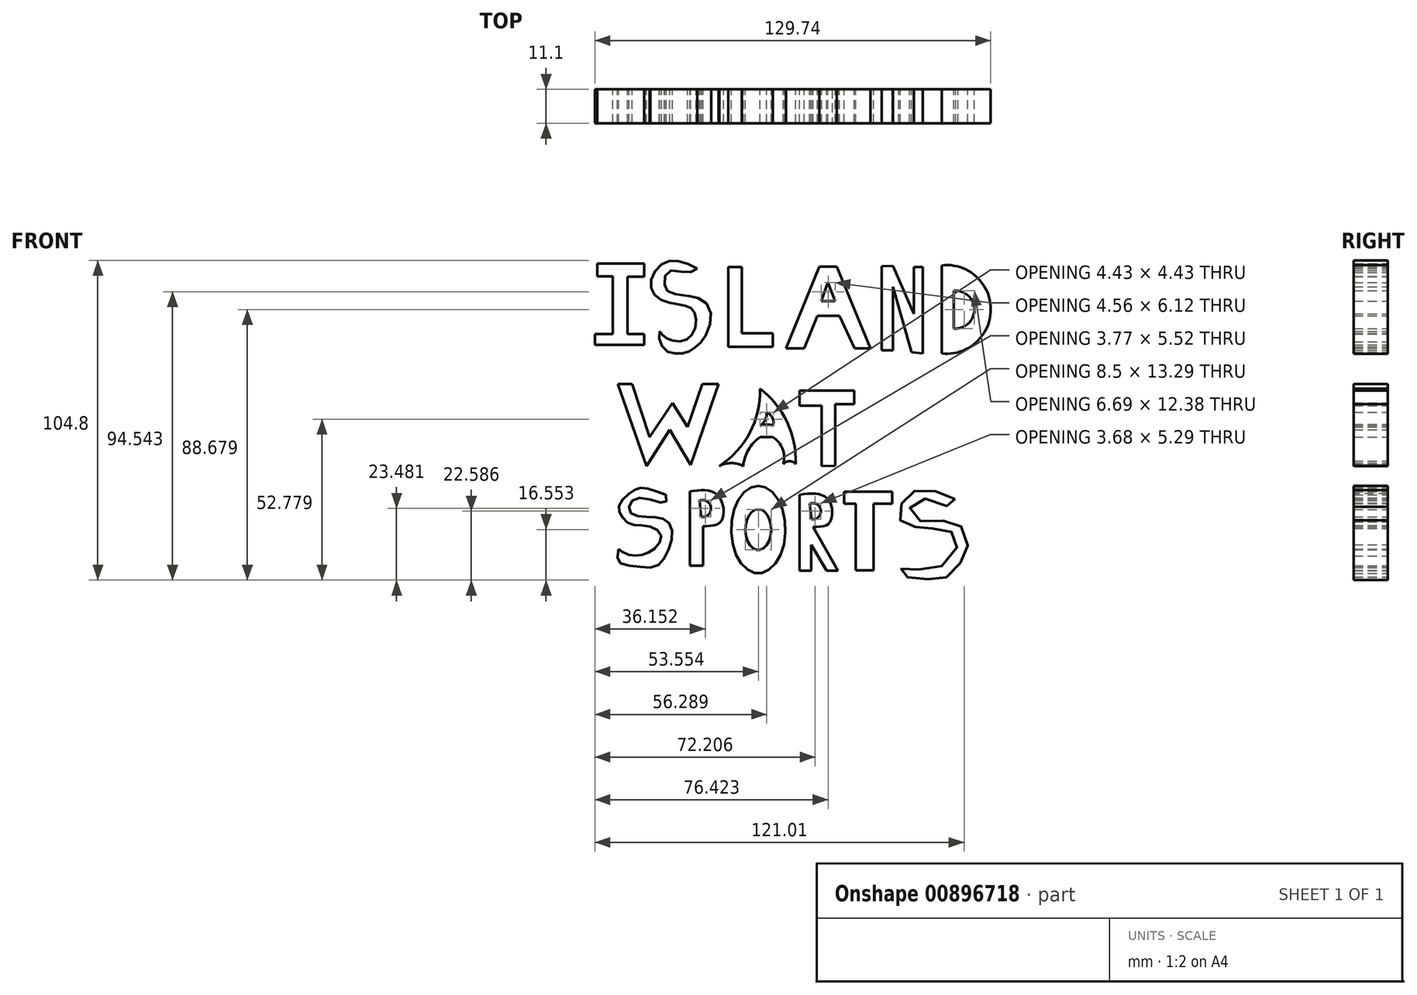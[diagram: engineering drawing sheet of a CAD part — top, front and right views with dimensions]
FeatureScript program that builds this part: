
annotation { "Feature Type Name" : "Feature", "Feature Type Description" : "" }
export const myFeature = defineFeature(function(context is Context, id is Id, definition is map)
    precondition{}
    {
        {
            var Q0;
            Q0=qCreatedBy(makeId("Front.planeOp"),FACE);
            var sketch = newSketch(context, id + "F0", { "sketchPlane" : qUnion([Q0])});
            skLineSegment(sketch, "E0", {"start": v(-52.45, 52.71) * mm, "end": v(-52.45, 33.82) * mm});
            skLineSegment(sketch, "E1", {"start": v(-52.45, 33.82) * mm, "end": v(-58.31, 33.82) * mm});
            skLineSegment(sketch, "E2", {"start": v(-58.31, 33.82) * mm, "end": v(-58.31, 30.3) * mm});
            skLineSegment(sketch, "E3", {"start": v(-58.31, 30.3) * mm, "end": v(-42.16, 30.3) * mm});
            skLineSegment(sketch, "E4", {"start": v(-42.16, 30.3) * mm, "end": v(-42.16, 33.82) * mm});
            skLineSegment(sketch, "E5", {"start": v(-42.16, 33.82) * mm, "end": v(-47.63, 33.82) * mm});
            skLineSegment(sketch, "E6", {"start": v(-47.63, 33.82) * mm, "end": v(-47.63, 52.58) * mm});
            skLineSegment(sketch, "E7", {"start": v(-47.63, 52.58) * mm, "end": v(-42.16, 52.58) * mm});
            skLineSegment(sketch, "E8", {"start": v(-52.45, 52.71) * mm, "end": v(-57.53, 52.71) * mm});
            skLineSegment(sketch, "E9", {"start": v(-57.53, 52.71) * mm, "end": v(-57.53, 56.88) * mm});
            skLineSegment(sketch, "E10", {"start": v(-57.53, 56.88) * mm, "end": v(-42.16, 56.88) * mm});
            skLineSegment(sketch, "E11", {"start": v(-42.16, 56.88) * mm, "end": v(-42.16, 52.58) * mm});
            skFitSpline(sketch, "E12", {"points": [v(-24.82, 55.32) * mm, v(-34.47, 57.66) * mm, v(-40.07, 50.63) * mm, v(-36.55, 45.02) * mm, v(-29, 43.2) * mm, v(-25.6, 40.85) * mm, v(-26, 34.34) * mm, v(-30.56, 31.34) * mm, v(-35.5, 32.9) * mm, v(-37.07, 34.73) * mm], "startDerivative": vector(-70.48, 35.1) * mm, "endDerivative": vector(-16.93, 26.6) * mm});
            skFitSpline(sketch, "E13", {"points": [v(-37.07, 34.73) * mm, v(-37.07, 31.34) * mm, v(-34.6, 28.08) * mm, v(-31.34, 27.43) * mm, v(-28.34, 27.7) * mm, v(-25.21, 29.65) * mm, v(-23, 31.73) * mm, v(-20.26, 38.77) * mm, v(-22.6, 44.63) * mm, v(-27.7, 46.33) * mm, v(-29.78, 46.59) * mm, v(-34.2, 47.63) * mm, v(-35.5, 50.36) * mm, v(-34.2, 54.4) * mm, v(-27.95, 54.01) * mm, v(-24.82, 55.32) * mm], "startDerivative": vector(-8.29, -55.15) * mm, "endDerivative": vector(42.75, 32.05) * mm});
            skLineSegment(sketch, "E14", {"start": v(-14.66, 55.84) * mm, "end": v(-14.66, 29.65) * mm});
            skLineSegment(sketch, "E15", {"start": v(-14.66, 29.65) * mm, "end": v(0, 29.65) * mm});
            skLineSegment(sketch, "E16", {"start": v(0, 29.65) * mm, "end": v(0, 34.08) * mm});
            skLineSegment(sketch, "E17", {"start": v(0, 34.08) * mm, "end": v(-10.23, 34.08) * mm});
            skLineSegment(sketch, "E18", {"start": v(-10.23, 34.08) * mm, "end": v(-10.23, 55.84) * mm});
            skLineSegment(sketch, "E19", {"start": v(-10.23, 55.84) * mm, "end": v(-14.66, 55.84) * mm});
            skLineSegment(sketch, "E20", {"start": v(15.18, 55.97) * mm, "end": v(4.37, 29.12) * mm});
            skLineSegment(sketch, "E21", {"start": v(4.37, 29.12) * mm, "end": v(10.23, 29.12) * mm});
            skLineSegment(sketch, "E22", {"start": v(10.23, 29.12) * mm, "end": v(14.66, 39.8) * mm});
            skLineSegment(sketch, "E23", {"start": v(14.66, 39.8) * mm, "end": v(21.83, 39.8) * mm});
            skLineSegment(sketch, "E24", {"start": v(21.83, 39.8) * mm, "end": v(26.78, 29.12) * mm});
            skLineSegment(sketch, "E25", {"start": v(26.78, 29.12) * mm, "end": v(32, 29.12) * mm});
            skLineSegment(sketch, "E26", {"start": v(32, 29.12) * mm, "end": v(20.91, 55.97) * mm});
            skLineSegment(sketch, "E27", {"start": v(20.91, 55.97) * mm, "end": v(15.18, 55.97) * mm});
            skLineSegment(sketch, "E28", {"start": v(15.83, 44.63) * mm, "end": v(20.4, 44.63) * mm});
            skLineSegment(sketch, "E29", {"start": v(20.4, 44.63) * mm, "end": v(18.05, 50.76) * mm});
            skLineSegment(sketch, "E30", {"start": v(18.05, 50.76) * mm, "end": v(15.83, 44.63) * mm});
            skLineSegment(sketch, "E31", {"start": v(35.64, 56.1) * mm, "end": v(35.64, 28.47) * mm});
            skLineSegment(sketch, "E32", {"start": v(35.64, 28.47) * mm, "end": v(39.42, 28.47) * mm});
            skLineSegment(sketch, "E33", {"start": v(39.42, 28.47) * mm, "end": v(39.42, 49.32) * mm});
            skLineSegment(sketch, "E34", {"start": v(49.2, 27.43) * mm, "end": v(49.2, 55.84) * mm});
            skLineSegment(sketch, "E35", {"start": v(49.2, 55.84) * mm, "end": v(46.2, 55.84) * mm});
            skLineSegment(sketch, "E36", {"start": v(46.2, 55.84) * mm, "end": v(46.2, 40.46) * mm});
            skLineSegment(sketch, "E37", {"start": v(46.2, 40.46) * mm, "end": v(39.42, 56.23) * mm});
            skLineSegment(sketch, "E38", {"start": v(39.42, 56.23) * mm, "end": v(35.64, 56.1) * mm});
            skLineSegment(sketch, "E39", {"start": v(39.42, 49.32) * mm, "end": v(45.41, 27.82) * mm});
            skLineSegment(sketch, "E40", {"start": v(45.41, 27.82) * mm, "end": v(49.2, 27.43) * mm});
            skLineSegment(sketch, "E41", {"start": v(55.32, 56.36) * mm, "end": v(55.32, 27.43) * mm});
            skArc(sketch, "E42", {"start": v(55.32, 27.43) * mm, "mid": v(71.43, 41.9) * mm, "end": v(55.32, 56.36) * mm});
            skLineSegment(sketch, "E43", {"start": v(59.36, 48.02) * mm, "end": v(59.36, 35.64) * mm});
            skArc(sketch, "E44", {"start": v(59.36, 35.64) * mm, "mid": v(66.04, 41.83) * mm, "end": v(59.36, 48.02) * mm});
            skLineSegment(sketch, "E45", {"start": v(-41.37, -9.45) * mm, "end": v(-33.82, 2.41) * mm});
            skLineSegment(sketch, "E46", {"start": v(-33.82, 2.41) * mm, "end": v(-26.9, -9.06) * mm});
            skLineSegment(sketch, "E47", {"start": v(-26.9, -9.06) * mm, "end": v(-17.79, 17.4) * mm});
            skLineSegment(sketch, "E48", {"start": v(-17.79, 17.4) * mm, "end": v(-23.13, 17.4) * mm});
            skLineSegment(sketch, "E49", {"start": v(-23.13, 17.4) * mm, "end": v(-27.98, 3.34) * mm});
            skLineSegment(sketch, "E50", {"start": v(-27.98, 3.34) * mm, "end": v(-32.9, 11.27) * mm});
            skLineSegment(sketch, "E51", {"start": v(-32.9, 11.27) * mm, "end": v(-40.33, 0) * mm});
            skLineSegment(sketch, "E52", {"start": v(-40.33, 0) * mm, "end": v(-46.06, 17.4) * mm});
            skLineSegment(sketch, "E53", {"start": v(-41.37, -9.45) * mm, "end": v(-50.76, 17.4) * mm});
            skLineSegment(sketch, "E54", {"start": v(-50.76, 17.4) * mm, "end": v(-46.06, 17.4) * mm});
            skArc(sketch, "E55", {"start": v(-17.53, -9.45) * mm, "mid": v(-7.52, 1.5) * mm, "end": v(-4.24, 15.96) * mm});
            skArc(sketch, "E56", {"start": v(7.5, -8.8) * mm, "mid": v(4.64, 5.01) * mm, "end": v(-4.24, 15.96) * mm});
            skArc(sketch, "E57", {"start": v(-9.7, -9.45) * mm, "mid": v(-13.62, -8.5) * mm, "end": v(-17.53, -9.45) * mm});
            skArc(sketch, "E58", {"start": v(-4.24, 0) * mm, "mid": v(-8, -4.13) * mm, "end": v(-9.7, -9.45) * mm});
            skLineSegment(sketch, "E59", {"start": v(-4.24, 0) * mm, "end": v(0, 0) * mm});
            skArc(sketch, "E60", {"start": v(3.45, -8.8) * mm, "mid": v(3.2, -3.82) * mm, "end": v(0, 0) * mm});
            skArc(sketch, "E61", {"start": v(7.5, -8.8) * mm, "mid": v(5.47, -7.88) * mm, "end": v(3.45, -8.8) * mm});
            skArc(sketch, "E62", {"start": v(-4.24, 3.71) * mm, "mid": v(-2.5, 5.62) * mm, "end": v(-2.02, 8.14) * mm});
            skArc(sketch, "E63", {"start": v(0, 3.71) * mm, "mid": v(-2.12, 4.17) * mm, "end": v(-4.24, 3.71) * mm});
            skArc(sketch, "E64", {"start": v(0, 3.71) * mm, "mid": v(-0.12, 6.34) * mm, "end": v(-2.02, 8.14) * mm});
            skLineSegment(sketch, "E65", {"start": v(15.96, -9.45) * mm, "end": v(15.96, 10.36) * mm});
            skLineSegment(sketch, "E66", {"start": v(15.96, 10.36) * mm, "end": v(8.8, 10.36) * mm});
            skLineSegment(sketch, "E67", {"start": v(8.8, 10.36) * mm, "end": v(8.8, 15.31) * mm});
            skLineSegment(sketch, "E68", {"start": v(8.8, 15.31) * mm, "end": v(26.65, 15.31) * mm});
            skLineSegment(sketch, "E69", {"start": v(26.65, 15.31) * mm, "end": v(26.65, 10.88) * mm});
            skLineSegment(sketch, "E70", {"start": v(26.65, 10.88) * mm, "end": v(20.4, 10.88) * mm});
            skLineSegment(sketch, "E71", {"start": v(20.4, 10.88) * mm, "end": v(20.4, -9.32) * mm});
            skLineSegment(sketch, "E72", {"start": v(20.4, -9.32) * mm, "end": v(15.96, -9.45) * mm});
            skLineSegment(sketch, "E73", {"start": v(30.56, 15.57) * mm, "end": v(30.56, -8.93) * mm});
            skLineSegment(sketch, "E74", {"start": v(30.56, -8.93) * mm, "end": v(40.6, -8.93) * mm});
            skLineSegment(sketch, "E75", {"start": v(40.6, -8.93) * mm, "end": v(40.6, -3.45) * mm});
            skLineSegment(sketch, "E76", {"start": v(40.6, -3.45) * mm, "end": v(34.2, -3.45) * mm});
            skLineSegment(sketch, "E77", {"start": v(34.2, -3.45) * mm, "end": v(34.2, 2.54) * mm});
            skLineSegment(sketch, "E78", {"start": v(34.2, 2.54) * mm, "end": v(39.03, 2.54) * mm});
            skLineSegment(sketch, "E79", {"start": v(39.03, 2.54) * mm, "end": v(39.03, 7.36) * mm});
            skLineSegment(sketch, "E80", {"start": v(39.03, 7.36) * mm, "end": v(34.08, 7.36) * mm});
            skLineSegment(sketch, "E81", {"start": v(34.08, 7.36) * mm, "end": v(34.08, 11.27) * mm});
            skLineSegment(sketch, "E82", {"start": v(34.08, 11.27) * mm, "end": v(40.6, 11.27) * mm});
            skLineSegment(sketch, "E83", {"start": v(40.6, 11.27) * mm, "end": v(40.6, 15.57) * mm});
            skLineSegment(sketch, "E84", {"start": v(40.6, 15.57) * mm, "end": v(30.56, 15.57) * mm});
            skLineSegment(sketch, "E85", {"start": v(44.9, 15.57) * mm, "end": v(44.9, -9.45) * mm});
            skLineSegment(sketch, "E86", {"start": v(44.9, -9.45) * mm, "end": v(44.9, 15.57) * mm});
            skFitSpline(sketch, "E87", {"points": [v(44.9, 15.57) * mm, v(50.5, 15.57) * mm, v(55.84, 12.05) * mm, v(58.57, 7.1) * mm, v(58.57, 2.8) * mm, v(53.75, 0) * mm, v(49.2, 0) * mm, v(49.45, 0) * mm], "startDerivative": vector(34.15, 4.52) * mm, "endDerivative": vector(11.25, -0.37) * mm});
            skLineSegment(sketch, "E88", {"start": v(49.45, 0) * mm, "end": v(57.14, -9.7) * mm});
            skLineSegment(sketch, "E89", {"start": v(57.14, -9.7) * mm, "end": v(51.54, -9.7) * mm});
            skLineSegment(sketch, "E90", {"start": v(51.54, -9.7) * mm, "end": v(48.02, -3.58) * mm});
            skLineSegment(sketch, "E91", {"start": v(48.02, -3.58) * mm, "end": v(48.02, -9.45) * mm});
            skLineSegment(sketch, "E92", {"start": v(48.02, -9.45) * mm, "end": v(44.9, -9.45) * mm});
            skArc(sketch, "E93", {"start": v(49.45, 4.1) * mm, "mid": v(53.9, 8) * mm, "end": v(49.58, 12.05) * mm});
            skLineSegment(sketch, "E94", {"start": v(49.58, 12.05) * mm, "end": v(49.45, 4.1) * mm});
            skFitSpline(sketch, "E95", {"points": [v(-35.12, -18.83) * mm, v(-42.55, -16.61) * mm, v(-46.2, -17.79) * mm, v(-50.36, -22.22) * mm, v(-49.84, -25.35) * mm, v(-46.59, -28.6) * mm, v(-40.72, -29.12) * mm, v(-36.55, -32.38) * mm, v(-38.9, -36.68) * mm, v(-43.2, -38.64) * mm, v(-47.5, -38.5) * mm, v(-50.5, -36.68) * mm, v(-50.5, -36.55) * mm], "startDerivative": vector(-72.28, 27.88) * mm, "endDerivative": vector(3.28, 7.09) * mm});
            skFitSpline(sketch, "E96", {"points": [v(-50.5, -36.55) * mm, v(-50.5, -40.85) * mm, v(-44.76, -42.42) * mm, v(-38.25, -42.29) * mm, v(-34.86, -38.25) * mm, v(-32.9, -31.34) * mm, v(-34.6, -27.56) * mm, v(-38.64, -26.26) * mm, v(-43.98, -25.87) * mm, v(-46.98, -24.3) * mm, v(-46.33, -21.04) * mm, v(-41.63, -20.13) * mm, v(-35.25, -21.44) * mm, v(-35.12, -18.83) * mm], "startDerivative": vector(-15.68, -68.6) * mm, "endDerivative": vector(-12.3, 59.6) * mm});
            skLineSegment(sketch, "E97", {"start": v(-27.17, -17.79) * mm, "end": v(-27.17, -42.16) * mm});
            skLineSegment(sketch, "E98", {"start": v(-27.17, -42.16) * mm, "end": v(-22.87, -42.16) * mm});
            skLineSegment(sketch, "E99", {"start": v(-22.87, -42.16) * mm, "end": v(-22.87, -29.12) * mm});
            skFitSpline(sketch, "E100", {"points": [v(-22.87, -29.12) * mm, v(-17.14, -27.82) * mm, v(-16.48, -21.96) * mm, v(-20, -17.79) * mm, v(-27.17, -17.79) * mm], "startDerivative": vector(27.8, 0.19) * mm, "endDerivative": vector(-28.78, -4.2) * mm});
            skArc(sketch, "E101", {"start": v(-23.52, -26.13) * mm, "mid": v(-20.27, -23.11) * mm, "end": v(-24.04, -20.78) * mm});
            skLineSegment(sketch, "E102", {"start": v(-24.04, -20.78) * mm, "end": v(-23.52, -26.13) * mm});
            skEllipse(sketch, "E103", {"center": v(-4.76, -30.3) * mm, "majorRadius": 14.33 * mm, "minorRadius": 8.9 * mm, "majorAxis": v(0, 1)});
            skEllipse(sketch, "E104", {"center": v(-4.76, -30.3) * mm, "majorRadius": 6.65 * mm, "minorRadius": 4.25 * mm, "majorAxis": v(0, 1)});
            skLineSegment(sketch, "E105", {"start": v(8.8, -18.83) * mm, "end": v(8.8, -43.72) * mm});
            skLineSegment(sketch, "E106", {"start": v(8.8, -43.72) * mm, "end": v(12.57, -43.72) * mm});
            skLineSegment(sketch, "E107", {"start": v(12.57, -43.72) * mm, "end": v(12.57, -35.25) * mm});
            skLineSegment(sketch, "E108", {"start": v(12.57, -35.25) * mm, "end": v(17.66, -43.72) * mm});
            skLineSegment(sketch, "E109", {"start": v(17.66, -43.72) * mm, "end": v(21.3, -43.72) * mm});
            skLineSegment(sketch, "E110", {"start": v(21.3, -43.72) * mm, "end": v(13.23, -29.38) * mm});
            skFitSpline(sketch, "E111", {"points": [v(8.8, -18.83) * mm, v(15.7, -18.83) * mm, v(18.96, -21.83) * mm, v(19.35, -25.87) * mm, v(18.05, -28.6) * mm, v(13.23, -29.38) * mm], "startDerivative": vector(30.5, 3.96) * mm, "endDerivative": vector(-27.36, -0.32) * mm});
            skArc(sketch, "E112", {"start": v(12.7, -26.9) * mm, "mid": v(15.74, -23.94) * mm, "end": v(12.05, -21.83) * mm});
            skLineSegment(sketch, "E113", {"start": v(12.05, -21.83) * mm, "end": v(12.7, -26.9) * mm});
            skLineSegment(sketch, "E114", {"start": v(27.17, -21.83) * mm, "end": v(27.17, -43.59) * mm});
            skLineSegment(sketch, "E115", {"start": v(27.17, -43.59) * mm, "end": v(33.03, -43.59) * mm});
            skLineSegment(sketch, "E116", {"start": v(33.03, -43.59) * mm, "end": v(33.03, -21.83) * mm});
            skLineSegment(sketch, "E117", {"start": v(33.03, -21.83) * mm, "end": v(39.16, -21.83) * mm});
            skLineSegment(sketch, "E118", {"start": v(39.16, -21.83) * mm, "end": v(39.16, -17.92) * mm});
            skLineSegment(sketch, "E119", {"start": v(39.16, -17.92) * mm, "end": v(23.4, -17.92) * mm});
            skLineSegment(sketch, "E120", {"start": v(23.4, -17.92) * mm, "end": v(23.4, -21.83) * mm});
            skLineSegment(sketch, "E121", {"start": v(23.4, -21.83) * mm, "end": v(27.17, -21.83) * mm});
            skFitSpline(sketch, "E122", {"points": [v(59.75, -20.26) * mm, v(52.58, -17.66) * mm, v(45.8, -17.92) * mm, v(42.02, -22.22) * mm, v(41.63, -27.04) * mm, v(45.41, -29.12) * mm, v(50.1, -29.9) * mm, v(55.97, -30.17) * mm, v(60.53, -33.03) * mm, v(57.92, -40.07) * mm, v(49.58, -43.72) * mm, v(42.68, -42.55) * mm, v(42.02, -45.54) * mm, v(46.46, -45.8) * mm, v(53.36, -46.85) * mm, v(58.44, -44.76) * mm, v(62.74, -39.16) * mm, v(63.79, -33.68) * mm, v(60, -27.82) * mm, v(52.97, -27.7) * mm, v(45.8, -26.13) * mm, v(45.54, -21.7) * mm, v(52.71, -20.65) * mm, v(58.7, -22.74) * mm, v(59.75, -20.26) * mm]});
            skLineSegment(sketch, "E123", {"start": v(-63.79, 62.74) * mm, "end": v(-62.48, -51.54) * mm});
            skLineSegment(sketch, "E124", {"start": v(-62.48, -51.54) * mm, "end": v(74.47, -52.71) * mm});
            skLineSegment(sketch, "E125", {"start": v(74.47, -52.71) * mm, "end": v(74.47, 61.44) * mm});
            skLineSegment(sketch, "E126", {"start": v(74.47, 61.44) * mm, "end": v(-63.79, 62.74) * mm});
            skArc(sketch, "E127", {"start": v(-63.79, 62.74) * mm, "mid": v(-55.89, 69.4) * mm, "end": v(-50.52, 78.22) * mm});
            skArc(sketch, "E128", {"start": v(-52.25, 62.64) * mm, "mid": v(-48.35, 70.1) * mm, "end": v(-50.52, 78.22) * mm});
            skArc(sketch, "E129", {"start": v(-52.25, 62.64) * mm, "mid": v(-41.84, 67.83) * mm, "end": v(-36.25, 78.03) * mm});
            skArc(sketch, "E130", {"start": v(-36.25, 62.64) * mm, "mid": v(-33.31, 70.33) * mm, "end": v(-36.25, 78.03) * mm});
            skArc(sketch, "E131", {"start": v(-36.25, 62.64) * mm, "mid": v(-24.78, 67.64) * mm, "end": v(-17.81, 78.03) * mm});
            skArc(sketch, "E132", {"start": v(-20.02, 62.33) * mm, "mid": v(-16.4, 69.83) * mm, "end": v(-17.81, 78.03) * mm});
            skArc(sketch, "E133", {"start": v(-20.02, 62.33) * mm, "mid": v(-8.26, 66.4) * mm, "end": v(-3.83, 78.03) * mm});
            skArc(sketch, "E134", {"start": v(0, 62.33) * mm, "mid": v(0.66, 70.81) * mm, "end": v(-3.83, 78.03) * mm});
            skArc(sketch, "E135", {"start": v(0, 62.33) * mm, "mid": v(8.7, 68.15) * mm, "end": v(12.16, 78.03) * mm});
            skArc(sketch, "E136", {"start": v(16, 62) * mm, "mid": v(16.7, 70.64) * mm, "end": v(12.16, 78.03) * mm});
            skArc(sketch, "E137", {"start": v(16, 62) * mm, "mid": v(24.7, 67.87) * mm, "end": v(29.48, 77.22) * mm});
            skArc(sketch, "E138", {"start": v(31.14, 61.85) * mm, "mid": v(33.3, 69.85) * mm, "end": v(29.48, 77.22) * mm});
            skArc(sketch, "E139", {"start": v(31.14, 61.85) * mm, "mid": v(38.47, 67.25) * mm, "end": v(41.67, 75.78) * mm});
            skArc(sketch, "E140", {"start": v(45.15, 61.72) * mm, "mid": v(45, 69.14) * mm, "end": v(41.67, 75.78) * mm});
            skArc(sketch, "E141", {"start": v(45.15, 61.72) * mm, "mid": v(53.3, 67.58) * mm, "end": v(56.14, 77.22) * mm});
            skArc(sketch, "E142", {"start": v(60.29, 61.57) * mm, "mid": v(60.6, 70.02) * mm, "end": v(56.14, 77.22) * mm});
            skArc(sketch, "E143", {"start": v(60.29, 61.57) * mm, "mid": v(67.55, 68.12) * mm, "end": v(71.12, 77.22) * mm});
            skArc(sketch, "E144", {"start": v(74.47, 61.44) * mm, "mid": v(75.38, 69.88) * mm, "end": v(71.12, 77.22) * mm});
            skLineSegment(sketch, "E145", {"start": v(-63.07, 0) * mm, "end": v(74.47, 0) * mm});
            skSolve(sketch);
        }
        {
            var Q0;
            Q0=makeQuery(id+"F0.imprint","IMPRINT",FACE,{"disambiguationData":[TD([[makeQuery(id+"F0.imprint","IMPRINT",EDGE,{"derivedFrom":sQuery(id+"F0.wireOp",EDGE,"E0")}),1.0]])]});
            var Q1;
            Q1=makeQuery(id+"F0.imprint","IMPRINT",FACE,{"disambiguationData":[TD([[makeQuery(id+"F0.imprint","IMPRINT",EDGE,{"derivedFrom":sQuery(id+"F0.wireOp",EDGE,"E12")}),1.0]])]});
            var Q2;
            {var subQ0=sQuery(id+"F0.wireOp",EDGE,"E96");var subQ1=sQuery(id+"F0.wireOp",EDGE,"E95");var subQ2=makeQuery(id+"F0.imprint","INTERSECT",VERTEX,{"disambiguationData":[OD(0.0)],"derivedFrom":[subQ1,subQ0]});Q2=makeQuery(id+"F0.imprint","IMPRINT",FACE,{"disambiguationData":[TD([[makeQuery(id+"F0.imprint","IMPRINT",EDGE,{"disambiguationData":[TD([[subQ2,-1.0]])],"derivedFrom":subQ1}),1.0]])]});}
            var Q3;
            Q3=makeQuery(id+"F0.imprint","IMPRINT",FACE,{"disambiguationData":[TD([[makeQuery(id+"F0.imprint","IMPRINT",EDGE,{"derivedFrom":sQuery(id+"F0.wireOp",EDGE,"E97")}),1.0]])]});
            var Q4;
            Q4=makeQuery(id+"F0.imprint","IMPRINT",FACE,{"disambiguationData":[TD([[makeQuery(id+"F0.imprint","IMPRINT",EDGE,{"derivedFrom":sQuery(id+"F0.wireOp",EDGE,"E103")}),1.0]])]});
            var Q5;
            Q5=makeQuery(id+"F0.imprint","IMPRINT",FACE,{"disambiguationData":[TD([[makeQuery(id+"F0.imprint","IMPRINT",EDGE,{"derivedFrom":sQuery(id+"F0.wireOp",EDGE,"E105")}),1.0]])]});
            var Q6;
            Q6=makeQuery(id+"F0.imprint","IMPRINT",FACE,{"disambiguationData":[TD([[makeQuery(id+"F0.imprint","IMPRINT",EDGE,{"derivedFrom":sQuery(id+"F0.wireOp",EDGE,"E114")}),1.0]])]});
            var Q7;
            Q7=makeQuery(id+"F0.imprint","IMPRINT",FACE,{"disambiguationData":[TD([[makeQuery(id+"F0.imprint","IMPRINT",EDGE,{"derivedFrom":sQuery(id+"F0.wireOp",EDGE,"E122")}),1.0]])]});
            var Q8;
            Q8=makeQuery(id+"F0.imprint","IMPRINT",FACE,{"disambiguationData":[TD([[makeQuery(id+"F0.imprint","IMPRINT",EDGE,{"derivedFrom":sQuery(id+"F0.wireOp",EDGE,"E14")}),1.0]])]});
            var Q9;
            Q9=makeQuery(id+"F0.imprint","IMPRINT",FACE,{"disambiguationData":[TD([[makeQuery(id+"F0.imprint","IMPRINT",EDGE,{"derivedFrom":sQuery(id+"F0.wireOp",EDGE,"E20")}),1.0]])]});
            var Q10;
            Q10=makeQuery(id+"F0.imprint","IMPRINT",FACE,{"disambiguationData":[TD([[makeQuery(id+"F0.imprint","IMPRINT",EDGE,{"derivedFrom":sQuery(id+"F0.wireOp",EDGE,"E31")}),1.0]])]});
            var Q11;
            Q11=makeQuery(id+"F0.imprint","IMPRINT",FACE,{"disambiguationData":[TD([[makeQuery(id+"F0.imprint","IMPRINT",EDGE,{"derivedFrom":sQuery(id+"F0.wireOp",EDGE,"E41")}),1.0]])]});
            var Q12;
            {var subQ0=sQuery(id+"F0.wireOp",EDGE,"E52");Q12=makeQuery(id+"F0.imprint","IMPRINT",FACE,{"disambiguationData":[TD([[makeQuery(id+"F0.imprint","IMPRINT",EDGE,{"derivedFrom":subQ0}),1.0]])]});}
            var Q13;
            {var subQ0=sQuery(id+"F0.wireOp",EDGE,"E53");var subQ1=sQuery(id+"F0.wireOp",EDGE,"E45");var subQ2=makeQuery(id+"F0.imprint","INTERSECT",VERTEX,{"derivedFrom":[subQ1,subQ0]});Q13=makeQuery(id+"F0.imprint","IMPRINT",FACE,{"disambiguationData":[TD([[makeQuery(id+"F0.imprint","IMPRINT",EDGE,{"disambiguationData":[TD([[subQ2,-1.0]])],"derivedFrom":subQ1}),1.0]])]});}
            var Q14;
            {var subQ0=sQuery(id+"F0.wireOp",EDGE,"E47");var subQ1=sQuery(id+"F0.wireOp",EDGE,"E46");var subQ2=makeQuery(id+"F0.imprint","INTERSECT",VERTEX,{"derivedFrom":[subQ1,subQ0]});Q14=makeQuery(id+"F0.imprint","IMPRINT",FACE,{"disambiguationData":[TD([[makeQuery(id+"F0.imprint","IMPRINT",EDGE,{"disambiguationData":[TD([[subQ2,1.0]])],"derivedFrom":subQ1}),1.0]])]});}
            var Q15;
            {var subQ0=sQuery(id+"F0.wireOp",EDGE,"E48");Q15=makeQuery(id+"F0.imprint","IMPRINT",FACE,{"disambiguationData":[TD([[makeQuery(id+"F0.imprint","IMPRINT",EDGE,{"derivedFrom":subQ0}),1.0]])]});}
            var Q16;
            Q16=makeQuery(id+"F0.imprint","IMPRINT",FACE,{"disambiguationData":[TD([[makeQuery(id+"F0.imprint","IMPRINT",EDGE,{"derivedFrom":sQuery(id+"F0.wireOp",EDGE,"E62")}),1.0]])]});
            var Q17;
            {var subQ0=sQuery(id+"F0.wireOp",EDGE,"E57");Q17=makeQuery(id+"F0.imprint","IMPRINT",FACE,{"disambiguationData":[TD([[makeQuery(id+"F0.imprint","IMPRINT",EDGE,{"derivedFrom":subQ0}),-1.0]])]});}
            var Q18;
            {var subQ4=sQuery(id+"F0.wireOp",EDGE,"E60");Q18=makeQuery(id+"F0.imprint","IMPRINT",FACE,{"disambiguationData":[TD([[makeQuery(id+"F0.imprint","IMPRINT",EDGE,{"derivedFrom":subQ4}),-1.0]])]});}
            var Q19;
            {var subQ0=sQuery(id+"F0.wireOp",EDGE,"E72");Q19=makeQuery(id+"F0.imprint","IMPRINT",FACE,{"disambiguationData":[TD([[makeQuery(id+"F0.imprint","IMPRINT",EDGE,{"derivedFrom":subQ0}),-1.0]])]});}
            var Q20;
            {var subQ0=sQuery(id+"F0.wireOp",EDGE,"E66");Q20=makeQuery(id+"F0.imprint","IMPRINT",FACE,{"disambiguationData":[TD([[makeQuery(id+"F0.imprint","IMPRINT",EDGE,{"derivedFrom":subQ0}),-1.0]])]});}
            extrude(context, id + "F1", {"entities" : qUnion([Q0, Q1, Q2, Q3, Q4, Q5, Q6, Q7, Q8, Q9, Q10, Q11, Q12, Q13, Q14, Q15, Q16, Q17, Q18, Q19, Q20]), "depth" : 11.1 * mm, "offsetDistance" : 25 * mm});
        }
    });
